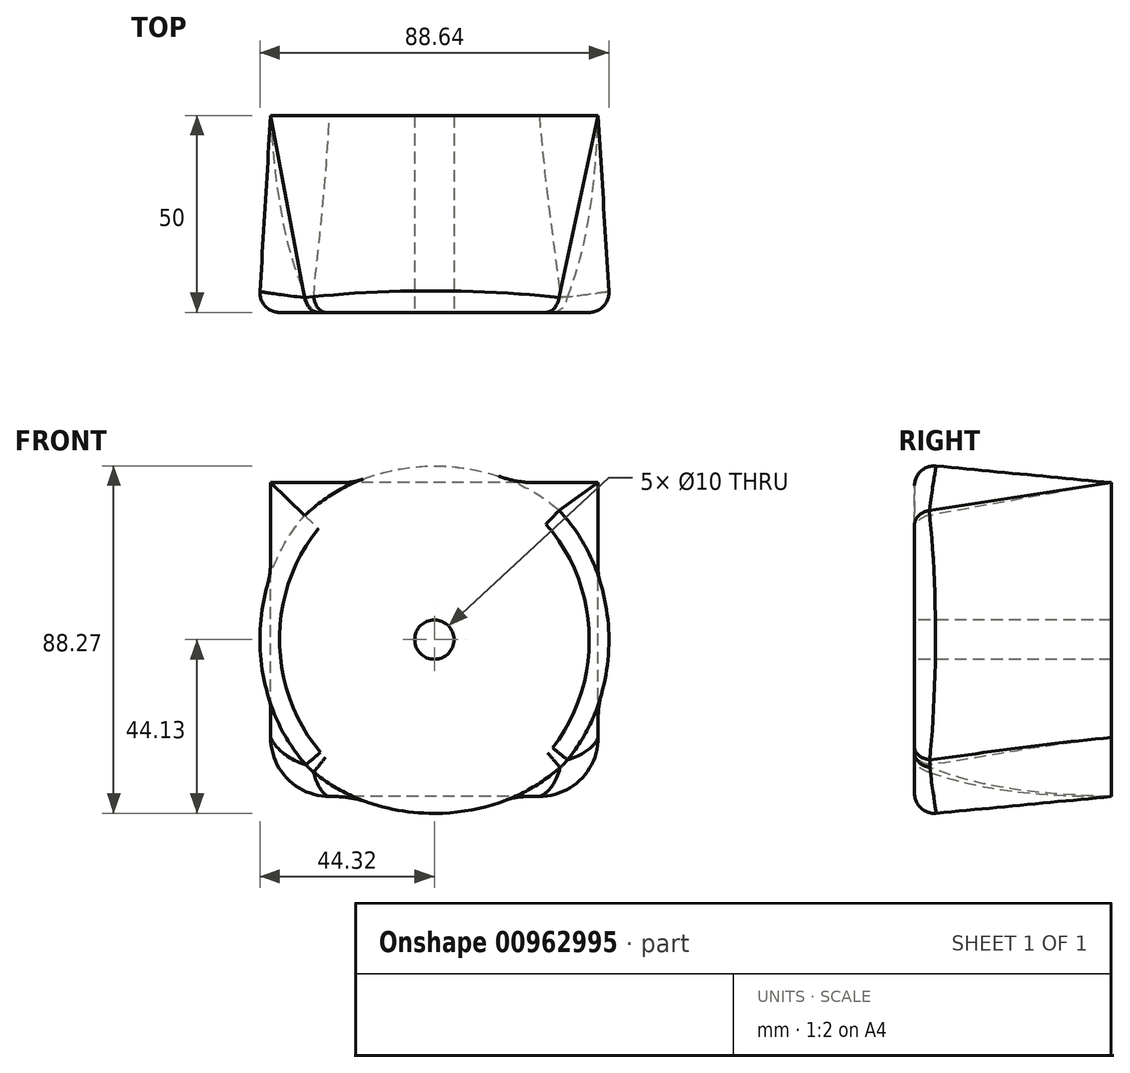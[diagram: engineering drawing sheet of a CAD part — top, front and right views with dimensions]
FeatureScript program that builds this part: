
annotation { "Feature Type Name" : "Feature", "Feature Type Description" : "" }
export const myFeature = defineFeature(function(context is Context, id is Id, definition is map)
    precondition{}
    {
        {
            var Q0;
            Q0=qCreatedBy(makeId("Front.planeOp"),FACE);
            var sketch = newSketch(context, id + "F0", { "sketchPlane" : qUnion([Q0])});
            skLineSegment(sketch, "E0.bottom", {"start": v(41.6, -39.87) * mm, "end": v(-41.6, -39.87) * mm});
            skLineSegment(sketch, "E0.top", {"start": v(41.6, 39.87) * mm, "end": v(-41.6, 39.87) * mm});
            skLineSegment(sketch, "E0.left", {"start": v(41.6, -39.87) * mm, "end": v(41.6, 39.87) * mm});
            skLineSegment(sketch, "E0.right", {"start": v(-41.6, -39.87) * mm, "end": v(-41.6, 39.87) * mm});
            skPoint(sketch, "E0.middle", {"position": v(0, 0) * mm});
            skSolve(sketch);
        }
        {
            var Q0;
            Q0=qCreatedBy(makeId("Front.planeOp"),FACE);
            cPlane(context, id + "F1", {"entities" : qUnion([Q0]), "cplaneType" : CPlaneType.OFFSET, "offset" : 50 * mm, "width" : 152.4 * mm, "height" : 152.4 * mm});
        }
        {
            var Q0;
            Q0=qCreatedBy(id+"F1.planeOp",FACE);
            var sketch = newSketch(context, id + "F2", { "sketchPlane" : qUnion([Q0])});
            skCircle(sketch, "E1", {"center": v(0, 0) * mm, "radius": 44.63 * mm});
            skSolve(sketch);
        }
        {
            var Q0;
            Q0=makeQuery(id+"F0.imprint","IMPRINT",FACE,{"disambiguationData":[TD([[makeQuery(id+"F0.imprint","IMPRINT",EDGE,{"derivedFrom":sQuery(id+"F0.wireOp",EDGE,"E0.bottom")}),-1.0]])]});
            var Q1;
            Q1=makeQuery(id+"F2.imprint","IMPRINT",FACE,{"disambiguationData":[TD([[makeQuery(id+"F2.imprint","IMPRINT",EDGE,{"derivedFrom":sQuery(id+"F2.wireOp",EDGE,"E1")}),1.0]])]});
            loft(context, id + "F3", {"sheetProfilesArray" : [{ "sheetProfileEntities" : qUnion([Q0]) }, { "sheetProfileEntities" : qUnion([Q1]) }]});
        }
        {
            var Q0;
            Q0=makeQuery(id+"F3.opLoft","SWEPT_EDGE",EDGE,{"disambiguationData":[OSD([sQuery(id+"F0.wireOp",EDGE,"E0.bottom"),sQuery(id+"F0.wireOp",EDGE,"E0.left")])]});
            var Q1;
            Q1=makeQuery(id+"F3.opLoft","SWEPT_EDGE",EDGE,{"disambiguationData":[OSD([sQuery(id+"F0.wireOp",EDGE,"E0.bottom"),sQuery(id+"F0.wireOp",EDGE,"E0.top"),sQuery(id+"F0.wireOp",EDGE,"E0.right"),sQuery(id+"F2.wireOp",EDGE,"E1")])]});
            fillet(context, id + "F4", {"entities" : qUnion([Q0, Q1]), "radius" : 15 * mm, "tangentPropagation" : true, "allowEdgeOverflow" : false});
        }
        {
            var Q0;
            Q0=makeQuery(id+"F3.opLoft","MID_CAP_EDGE",EDGE,{"disambiguationData":[OSD([sQuery(id+"F0.wireOp",EDGE,"E0.top"),sQuery(id+"F0.wireOp",EDGE,"E0.left"),sQuery(id+"F0.wireOp",EDGE,"E0.right"),sQuery(id+"F2.wireOp",EDGE,"E1")])],"capPos":1.0});
            var Q1;
            Q1=makeQuery(id+"F3.opLoft","MID_CAP_EDGE",EDGE,{"disambiguationData":[OSD([sQuery(id+"F0.wireOp",EDGE,"E0.bottom"),sQuery(id+"F0.wireOp",EDGE,"E0.top"),sQuery(id+"F0.wireOp",EDGE,"E0.left"),sQuery(id+"F2.wireOp",EDGE,"E1")])],"capPos":1.0});
            fillet(context, id + "F5", {"entities" : qUnion([Q0, Q1]), "radius" : 5 * mm, "tangentPropagation" : true, "allowEdgeOverflow" : false});
        }
        {
            var Q0;
            Q0=makeQuery(id+"F3.opLoft","CAP_FACE",FACE,{"disambiguationData":[OSD([makeQuery(id+"F2.imprint","IMPRINT",FACE,{"disambiguationData":[TD([[makeQuery(id+"F2.imprint","IMPRINT",EDGE,{"derivedFrom":sQuery(id+"F2.wireOp",EDGE,"E1")}),1.0]])]})])],"isStart":true});
            var Q1;
            Q1=qCreatedBy(id+"F1.planeOp",FACE);
            var sketch = newSketch(context, id + "F6", { "sketchPlane" : qUnion([Q0, Q1])});
            skCircle(sketch, "E2", {"center": v(0, 0) * mm, "radius": 5 * mm});
            skSolve(sketch);
        }
        {
            var Q0;
            Q0=makeQuery(id+"F6.imprint","IMPRINT",FACE,{"disambiguationData":[TD([[makeQuery(id+"F6.imprint","IMPRINT",EDGE,{"derivedFrom":sQuery(id+"F6.wireOp",EDGE,"E2")}),1.0]])]});
            extrude(context, id + "F7", {"entities" : qUnion([Q0]), "operationType" : NewBodyOperationType.REMOVE, "oppositeDirection" : true, "depth" : 100 * mm, "offsetDistance" : 25 * mm});
        }
    });
